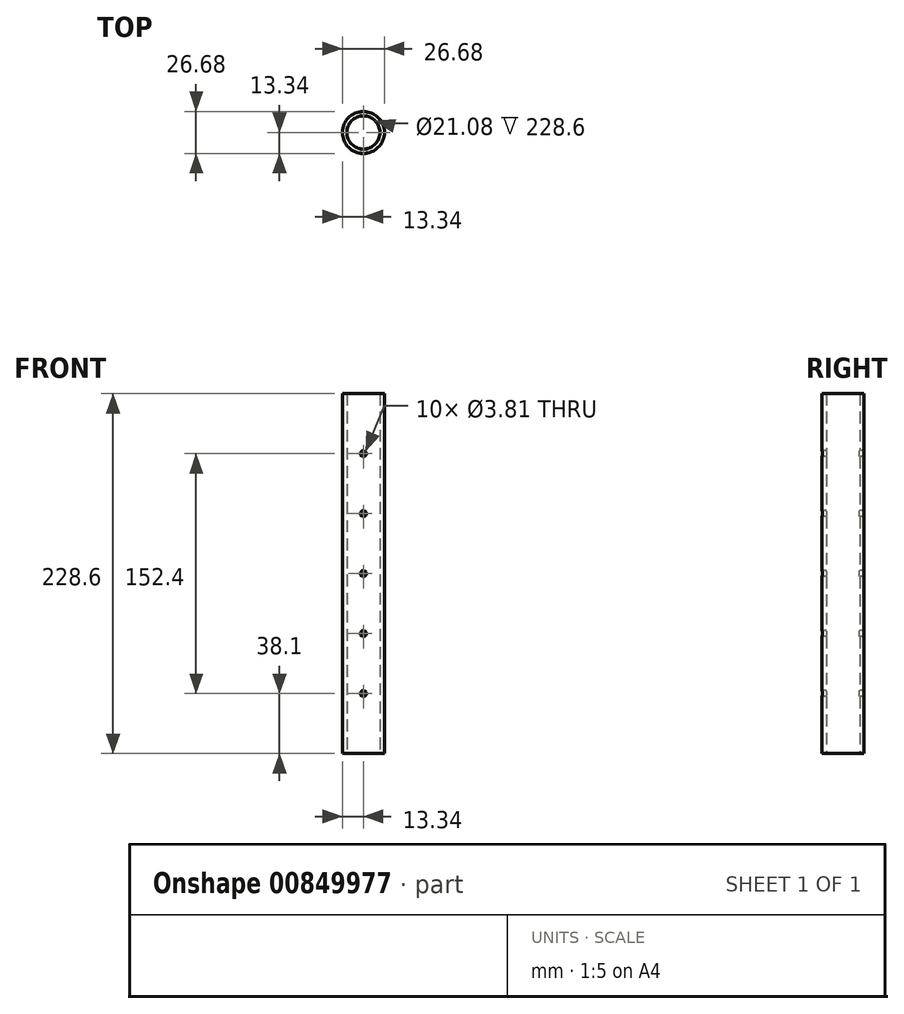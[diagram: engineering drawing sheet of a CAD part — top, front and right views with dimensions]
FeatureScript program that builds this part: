
annotation { "Feature Type Name" : "Feature", "Feature Type Description" : "" }
export const myFeature = defineFeature(function(context is Context, id is Id, definition is map)
    precondition{}
    {
        {
            var Q0;
            Q0=qCreatedBy(makeId("Top.planeOp"),FACE);
            var sketch = newSketch(context, id + "F0", { "sketchPlane" : qUnion([Q0])});
            skCircle(sketch, "E0", {"center": v(0, 0) * mm, "radius": 10.54 * mm});
            skCircle(sketch, "E1", {"center": v(0, 0) * mm, "radius": 13.34 * mm});
            skSolve(sketch);
        }
        {
            var Q0;
            Q0 = qSketchRegion(id + "F0", true);
            extrude(context, id + "F1", {"entities" : qUnion([Q0]), "depth" : 228.6 * mm, "offsetDistance" : 25.4 * mm});
        }
        {
            var Q0;
            Q0=qCreatedBy(makeId("Front.planeOp"),FACE);
            var sketch = newSketch(context, id + "F2", { "sketchPlane" : qUnion([Q0])});
            skCircle(sketch, "E2", {"center": v(0, 38.1) * mm, "radius": 1.9 * mm});
            skCircle(sketch, "E3.0.1.0", {"center": v(0, 76.2) * mm, "radius": 1.9 * mm});
            skCircle(sketch, "E3.0.2.0", {"center": v(0, 114.3) * mm, "radius": 1.9 * mm});
            skCircle(sketch, "E3.0.3.0", {"center": v(0, 152.4) * mm, "radius": 1.9 * mm});
            skCircle(sketch, "E3.0.4.0", {"center": v(0, 190.5) * mm, "radius": 1.9 * mm});
            skLineSegment(sketch, "E3.direction1", {"start": v(0, 38.1) * mm, "end": v(69.34, 38.1) * mm, "construction": true});
            skLineSegment(sketch, "E3.direction2", {"start": v(0, 38.1) * mm, "end": v(0, 76.2) * mm, "construction": true});
            skSolve(sketch);
        }
        {
            var Q0;
            Q0 = qSketchRegion(id + "F2", true);
            extrude(context, id + "F3", {"entities" : qUnion([Q0]), "operationType" : NewBodyOperationType.REMOVE, "endBound" : BoundingType.THROUGH_ALL, "oppositeDirection" : true, "depth" : 25.4 * mm, "offsetDistance" : 25.4 * mm, "hasSecondDirection" : true, "secondDirectionBound" : SecondDirectionBoundingType.THROUGH_ALL, "secondDirectionOppositeDirection" : false, "secondDirectionDepth" : 64.77 * mm});
        }
    });
